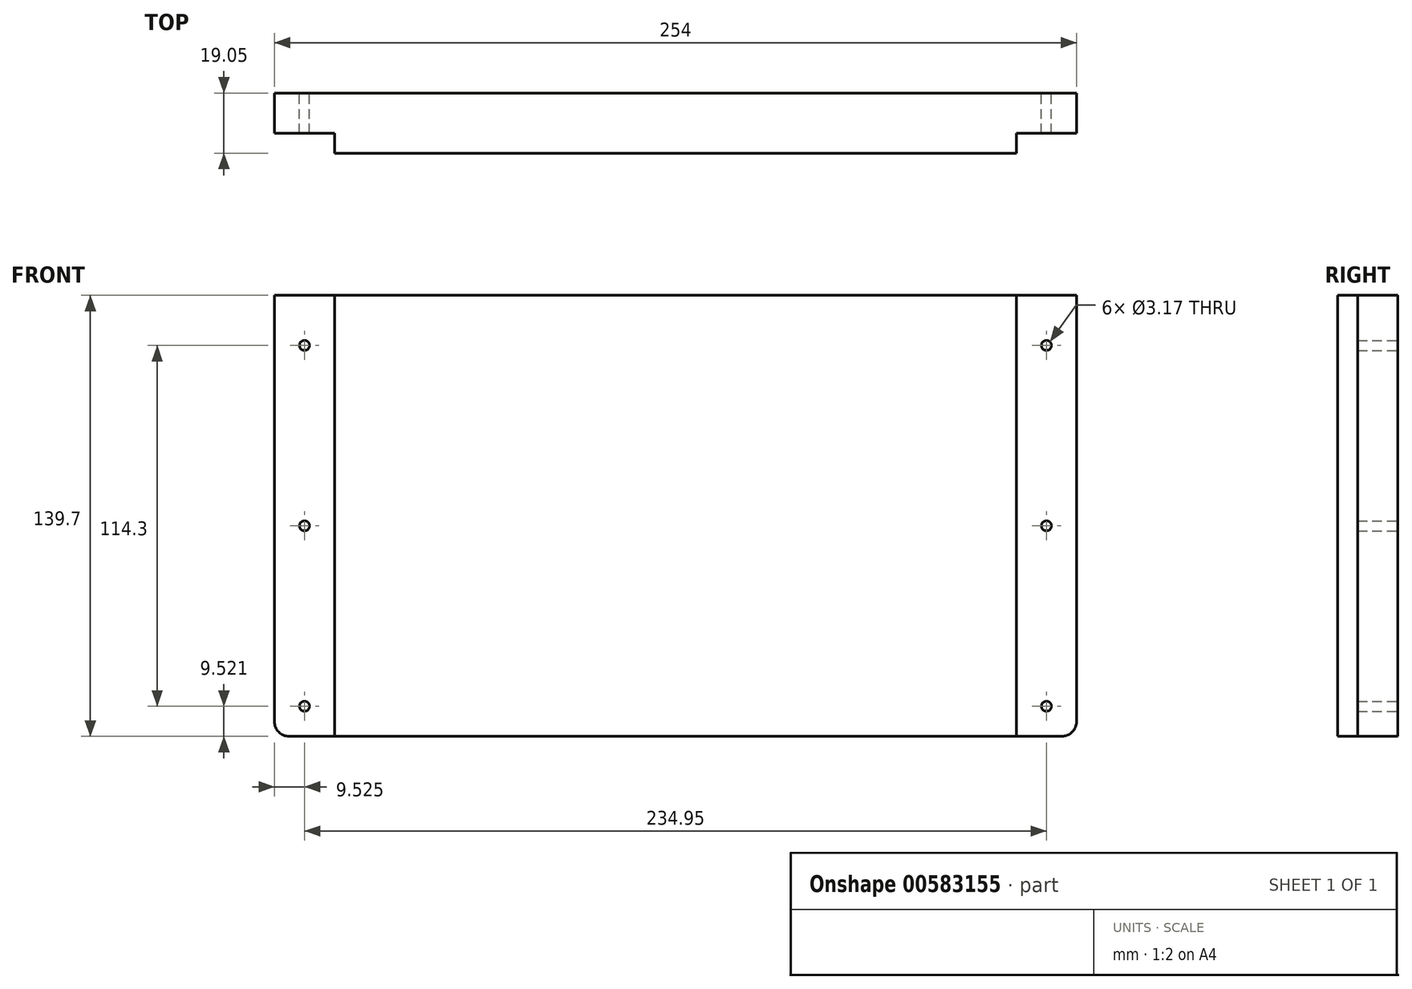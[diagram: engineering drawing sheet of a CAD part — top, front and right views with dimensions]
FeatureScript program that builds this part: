
annotation { "Feature Type Name" : "Feature", "Feature Type Description" : "" }
export const myFeature = defineFeature(function(context is Context, id is Id, definition is map)
    precondition{}
    {
        {
            var Q0;
            Q0=qCreatedBy(makeId("Front.planeOp"),FACE);
            var sketch = newSketch(context, id + "F0", { "sketchPlane" : qUnion([Q0])});
            skLineSegment(sketch, "E0.top", {"start": v(27.94, 164.85) * mm, "end": v(281.94, 164.85) * mm});
            skLineSegment(sketch, "E1", {"start": v(27.94, 164.85) * mm, "end": v(27.94, 29.83) * mm});
            skLineSegment(sketch, "E2", {"start": v(32.63, 25.15) * mm, "end": v(277.25, 25.15) * mm});
            skLineSegment(sketch, "E3", {"start": v(46.99, 164.85) * mm, "end": v(46.99, 25.15) * mm});
            skLineSegment(sketch, "E4", {"start": v(262.89, 164.85) * mm, "end": v(262.89, 25.15) * mm});
            skCircle(sketch, "E5.MirrorC", {"center": v(37.46, 148.97) * mm, "radius": 1.59 * mm});
            skCircle(sketch, "E6.MirrorC", {"center": v(37.46, 34.67) * mm, "radius": 1.59 * mm});
            skCircle(sketch, "E7.MirrorC", {"center": v(37.46, 91.82) * mm, "radius": 1.59 * mm});
            skLineSegment(sketch, "E8", {"start": v(281.94, 164.85) * mm, "end": v(281.94, 29.83) * mm});
            skCircle(sketch, "E9.MirrorC", {"center": v(272.41, 148.97) * mm, "radius": 1.59 * mm});
            skCircle(sketch, "E10.MirrorC", {"center": v(272.41, 34.67) * mm, "radius": 1.59 * mm});
            skCircle(sketch, "E11.MirrorC", {"center": v(272.41, 91.82) * mm, "radius": 1.59 * mm});
            skPoint(sketch, "E12.visualSharp", {"position": v(27.94, 25.15) * mm});
            skArc(sketch, "E12.filletArc", {"start": v(27.94, 29.83) * mm, "mid": v(29.31, 26.52) * mm, "end": v(32.63, 25.15) * mm});
            skPoint(sketch, "E13.visualSharp", {"position": v(281.94, 25.15) * mm});
            skArc(sketch, "E13.filletArc", {"start": v(277.25, 25.15) * mm, "mid": v(280.57, 26.52) * mm, "end": v(281.94, 29.83) * mm});
            skSolve(sketch);
        }
        {
            var Q0;
            Q0=makeQuery(id+"F0.imprint","IMPRINT",FACE,{"disambiguationData":[TD([[makeQuery(id+"F0.imprint","IMPRINT",EDGE,{"derivedFrom":sQuery(id+"F0.wireOp",EDGE,"E0.top")}),-1.0]])]});
            extrude(context, id + "F1", {"entities" : qUnion([Q0]), "depth" : 19.05 * mm, "offsetDistance" : 25.4 * mm});
        }
        {
            var Q0;
            {var subQ2=sQuery(id+"F0.wireOp",EDGE,"E1");Q0=makeQuery(id+"F0.imprint","IMPRINT",FACE,{"disambiguationData":[TD([[makeQuery(id+"F0.imprint","IMPRINT",EDGE,{"derivedFrom":subQ2}),1.0]])]});}
            var Q1;
            {var subQ2=sQuery(id+"F0.wireOp",EDGE,"E4");Q1=makeQuery(id+"F0.imprint","IMPRINT",FACE,{"disambiguationData":[TD([[makeQuery(id+"F0.imprint","IMPRINT",EDGE,{"derivedFrom":subQ2}),1.0]])]});}
            extrude(context, id + "F2", {"entities" : qUnion([Q0, Q1]), "operationType" : NewBodyOperationType.ADD, "depth" : 12.7 * mm, "offsetDistance" : 25.4 * mm});
        }
    });
